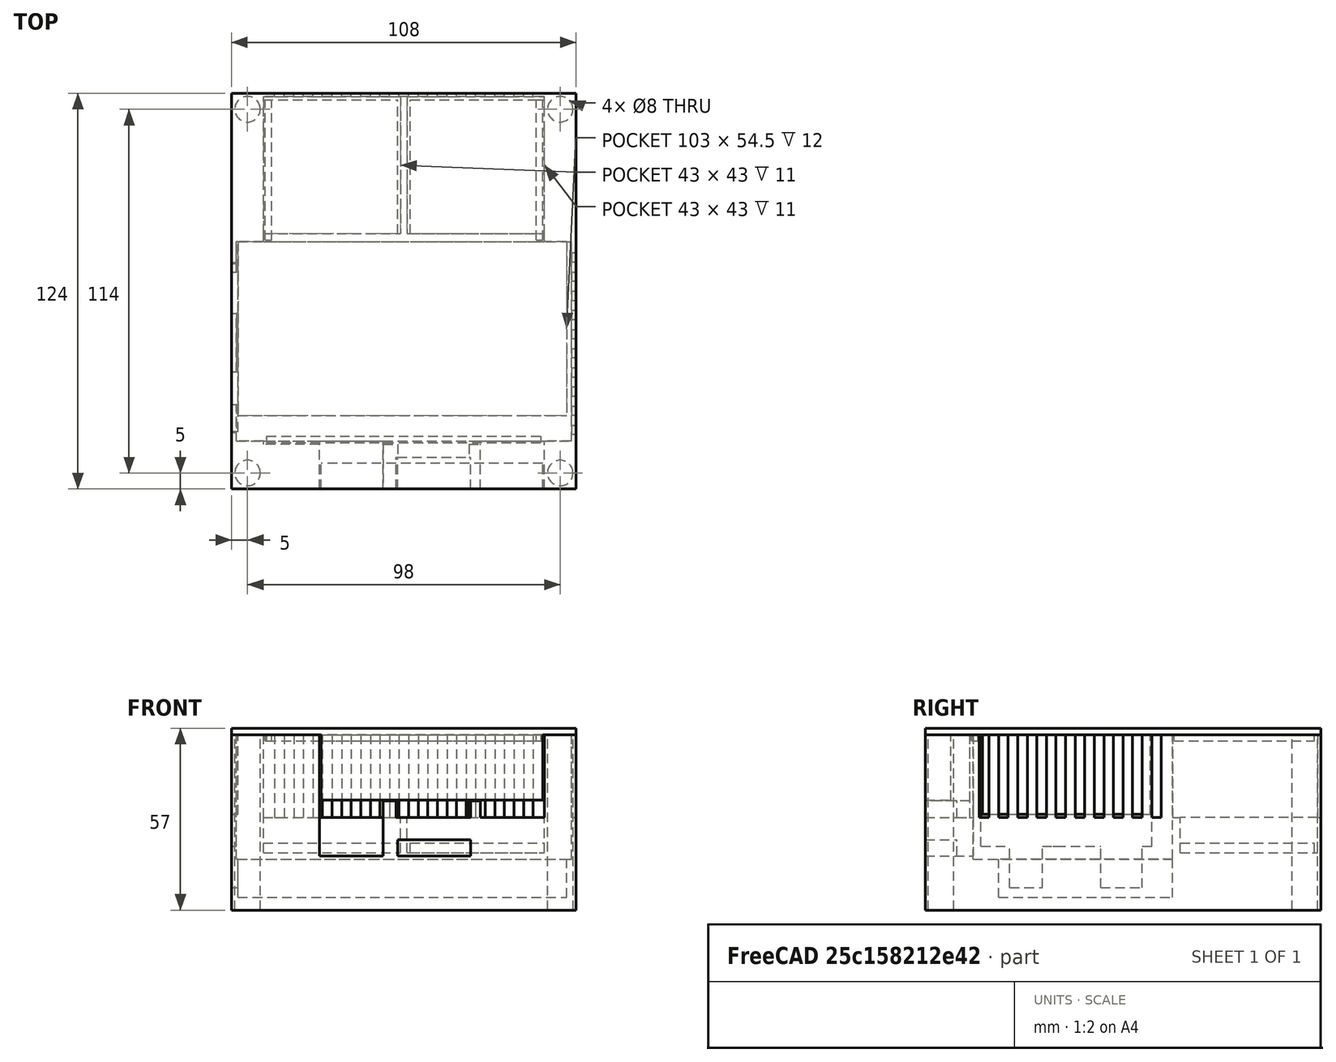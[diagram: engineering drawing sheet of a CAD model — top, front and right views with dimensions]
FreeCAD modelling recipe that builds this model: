
FCSTD DOCUMENT  (FreeCAD 0.19R24366 (Git))
Label: ORM-1 Controller Block
License: All rights reserved
LicenseURL: http://en.wikipedia.org/wiki/All_rights_reserved
objects: Part::Box×48, Part::Cut×15, Part::MultiFuse×6, Part::Cylinder×4, Mesh::Feature×2, App::MeasureDistance×2, Part::Compound×1
note: 74 computed .brp shape members not serialized (recipe doc carries the construction recipe); baked Part::Feature solids carry a one-line shape summary decoded from their .brp

FEATURE [Mesh::Feature] RAMPS1_4
  Placement = pos=(57,64,4) rot=(0,0,1;0rad)
FEATURE [Mesh::Feature] Fan_80mm
  Placement = pos=(6,13,84) rot=(0,0,1;0rad)
FEATURE [App::MeasureDistance] Distance  label="Distance: 78,43 mm"
  Distance = 78.426
  P1 = (81.5137,90.5618,25)
  P2 = (80.3884,12.1439,25)
FEATURE [Part::Box] Box  label="Encoders Jack"
  AttacherType = Attacher::AttachEngine3D
  Height = 5.08
  Length = 22.86
  Placement = pos=(52,0,17) rot=(0,0,1;0rad)
  Width = 10
  expr: Height = 2.54 * 2
  expr: Length = 2.54 * 9
FEATURE [Part::Box] Box001  label="ORM-1 CtrlBlock Main Volume"
  AttacherType = Attacher::AttachEngine3D
  Height = 55
  Length = 108
  Width = 124
FEATURE [Part::Box] Box002  label="A4988 Extension Board"
  AttacherType = Attacher::AttachEngine3D
  Height = 3
  Length = 42
  Placement = pos=(56,80,18) rot=(0,0,1;0rad)
  Width = 42
FEATURE [Part::Box] Box003  label="A4988 Extension Board001"
  AttacherType = Attacher::AttachEngine3D
  Height = 3
  Length = 42
  Placement = pos=(10,80,18) rot=(0,0,1;0rad)
  Width = 42
FEATURE [Part::Box] Box004  label="Arduino Board Socket"
  AttacherType = Attacher::AttachEngine3D
  Height = 100
  Length = 103
  Placement = pos=(2,23,4) rot=(0,0,1;0rad)
  Width = 54.5
FEATURE [Part::Cut] Cut  label="ORM-1 CTRL + ArduSocket"
  Base = -> Box001
  Tool = -> Box004
FEATURE [Part::Box] Box005  label="RAMPS1.4 Socket"
  AttacherType = Attacher::AttachEngine3D
  Height = 100
  Length = 105
  Placement = pos=(1.5,15,16) rot=(0,0,1;0rad)
  Width = 62.5
FEATURE [Part::Cut] Cut001  label="ORM-1 CTRL + Ramps Socket"
  Base = -> Cut
  Tool = -> Box005
FEATURE [Part::Box] Box006  label="A4988 Extension Board Socket"
  AttacherType = Attacher::AttachEngine3D
  Height = 100
  Length = 43
  Placement = pos=(55,80,18) rot=(0,0,1;0rad)
  Width = 43
FEATURE [Part::Box] Box007  label="A4988 Extension Board Socket001"
  AttacherType = Attacher::AttachEngine3D
  Height = 100
  Length = 43
  Placement = pos=(10,80,18) rot=(0,0,1;0rad)
  Width = 43
FEATURE [Part::Compound] Compound  label="A4988 Extension Board Sockets"
  Links = -> [Box006,Box007]
FEATURE [Part::Cut] Cut002  label="ORM-1 Controller Block. With A4988 Extension Board Sockets"
  Base = -> Cut001
  Tool = -> Compound
FEATURE [Part::Box] Box008  label="Encoders Jack Socket"
  AttacherType = Attacher::AttachEngine3D
  Height = 100
  Length = 23.36
  Placement = pos=(51.5,0,17) rot=(0,0,1;0rad)
  Width = 10
  expr: Length = 2.54 * 9 + 0.5
FEATURE [Part::Box] Box009  label="Encoders Jack Wires Socket"
  AttacherType = Attacher::AttachEngine3D
  Height = 100
  Length = 22.36
  Placement = pos=(52,0,17) rot=(0,0,1;0rad)
  Width = 16
  expr: Length = 2.54 * 9 - 0.5
FEATURE [Part::MultiFuse] Fusion  label="Encoder Jack Socket"
  Placement = pos=(0,0,12) rot=(0,0,1;0rad)
  Shapes = -> [Box008,Box009]
FEATURE [Part::Cut] Cut003  label="ORM-1 With Encoder Jack Socket"
  Base = -> Cut002
  Tool = -> Fusion
FEATURE [App::MeasureDistance] Distance001  label="Distance: 9,00 mm"
  Distance = 8.99628
  P1 = (69.3078,9.44422,17)
  P2 = (68.5344,0.481246,17)
FEATURE [Part::Box] Box010  label="Reset Button Socket"
  AttacherType = Attacher::AttachEngine3D
  Height = 100
  Length = 20
  Placement = pos=(27.5,0,17) rot=(0,0,1;0rad)
  Width = 17
FEATURE [Part::Cut] Cut004
  Base = -> Cut003
  Tool = -> Box010
FEATURE [Part::Box] Box011  label="USB Type B Socket"
  AttacherType = Attacher::AttachEngine3D
  Height = 100
  Length = 10
  Placement = pos=(0,55,7) rot=(0,0,1;0rad)
  Width = 13
FEATURE [Part::Cut] Cut005
  Base = -> Cut004
  Tool = -> Box011
FEATURE [Part::Box] Box012  label="Arduino Power Jack Socket"
  AttacherType = Attacher::AttachEngine3D
  Height = 100
  Length = 10
  Placement = pos=(0,26.5,7) rot=(0,0,1;0rad)
  Width = 10.2
FEATURE [Part::Cut] Cut006
  Base = -> Cut005
  Tool = -> Box012
FEATURE [Part::Box] Box013  label="RAMPS Input Power Socket"
  AttacherType = Attacher::AttachEngine3D
  Height = 100
  Length = 10
  Placement = pos=(0,17.5,20) rot=(0,0,1;0rad)
  Width = 23.5
FEATURE [Part::Cut] Cut007
  Base = -> Cut006
  Tool = -> Box013
FEATURE [Part::Box] Box014  label="RAMPS Output Power Socket"
  AttacherType = Attacher::AttachEngine3D
  Height = 100
  Length = 15
  Placement = pos=(0,40,20) rot=(0,0,1;0rad)
  Width = 31
FEATURE [Part::Cut] Cut008
  Base = -> Cut007
  Tool = -> Box014
FEATURE [Part::Box] Box015  label="Stepper Motors Wires Socket"
  AttacherType = Attacher::AttachEngine3D
  Height = 100
  Length = 20
  Placement = pos=(78,0,29) rot=(0,0,1;0rad)
  Width = 17
FEATURE [Part::Cut] Cut009
  Base = -> Cut008
  Tool = -> Box015
FEATURE [Part::Box] Box016  label="Excessive Volume Removal"
  AttacherType = Attacher::AttachEngine3D
  Height = 100
  Length = 88
  Placement = pos=(10,14,29) rot=(0,0,1;0rad)
  Width = 109
FEATURE [Part::Cut] Cut010
  Base = -> Cut009
  Tool = -> Box016
FEATURE [Part::Cylinder] Cylinder
  Angle = 360
  AttacherType = Attacher::AttachEngine3D
  Height = 100
  Placement = pos=(5,5,0) rot=(0,0,1;0rad)
  Radius = 4
FEATURE [Part::Cylinder] Cylinder001
  Angle = 360
  AttacherType = Attacher::AttachEngine3D
  Height = 100
  Placement = pos=(5,119,0) rot=(0,0,1;0rad)
  Radius = 4
FEATURE [Part::Cylinder] Cylinder002
  Angle = 360
  AttacherType = Attacher::AttachEngine3D
  Height = 100
  Placement = pos=(103,119,0) rot=(0,0,1;0rad)
  Radius = 4
FEATURE [Part::Cylinder] Cylinder003
  Angle = 360
  AttacherType = Attacher::AttachEngine3D
  Height = 100
  Placement = pos=(103,5,0) rot=(0,0,1;0rad)
  Radius = 4
FEATURE [Part::MultiFuse] Fusion001  label="Threaded Rivets Mounting Places"
  Shapes = -> [Cylinder,Cylinder001,Cylinder002,Cylinder003]
FEATURE [Part::Cut] Cut011
  Base = -> Cut010
  Tool = -> Fusion001
FEATURE [Part::Box] Box017  label="Extra Volume Removal"
  AttacherType = Attacher::AttachEngine3D
  Height = 100
  Length = 70.5
  Placement = pos=(27.5,0,34.2) rot=(0,0,1;0rad)
  Width = 19
  expr: .Placement.Base.z = 29 + 2.6 * 2
FEATURE [Part::Cut] Cut012
  Base = -> Cut011
  Tool = -> Box017
FEATURE [Part::Box] Box018  label="ORM-1 Controller Cover Main Volume"
  AttacherType = Attacher::AttachEngine3D
  Height = 2
  Length = 108
  Placement = pos=(0,0,55) rot=(0,0,1;0rad)
  Width = 124
FEATURE [Part::Box] Box019  label="Cube001"
  AttacherType = Attacher::AttachEngine3D
  Height = 21
  Length = 69.5
  Placement = pos=(28,0,34.5) rot=(0,0,1;0rad)
  Width = 8
FEATURE [Part::Box] Box020  label="Cube"
  AttacherType = Attacher::AttachEngine3D
  Height = 26
  Length = 2
  Placement = pos=(0,18,30) rot=(0,0,1;0rad)
  Width = 52.5
FEATURE [Part::Box] Box021  label="Cube002"
  AttacherType = Attacher::AttachEngine3D
  Height = 100
  Length = 10
  Placement = pos=(101,17,29) rot=(0,0,1;0rad)
  Width = 3
FEATURE [Part::Box] Box022  label="Cube003"
  AttacherType = Attacher::AttachEngine3D
  Height = 100
  Length = 10
  Placement = pos=(101,23,29) rot=(0,0,1;0rad)
  Width = 3
FEATURE [Part::Box] Box023  label="Cube004"
  AttacherType = Attacher::AttachEngine3D
  Height = 100
  Length = 10
  Placement = pos=(101,29,29) rot=(0,0,1;0rad)
  Width = 3
FEATURE [Part::Box] Box024  label="Cube005"
  AttacherType = Attacher::AttachEngine3D
  Height = 100
  Length = 10
  Placement = pos=(101,35,29) rot=(0,0,1;0rad)
  Width = 3
FEATURE [Part::Box] Box025  label="Cube006"
  AttacherType = Attacher::AttachEngine3D
  Height = 100
  Length = 10
  Placement = pos=(101,41,29) rot=(0,0,1;0rad)
  Width = 3
FEATURE [Part::Box] Box026  label="Cube007"
  AttacherType = Attacher::AttachEngine3D
  Height = 100
  Length = 10
  Placement = pos=(101,47,29) rot=(0,0,1;0rad)
  Width = 3
FEATURE [Part::Box] Box027  label="Cube008"
  AttacherType = Attacher::AttachEngine3D
  Height = 100
  Length = 10
  Placement = pos=(101,53,29) rot=(0,0,1;0rad)
  Width = 3
FEATURE [Part::Box] Box028  label="Cube009"
  AttacherType = Attacher::AttachEngine3D
  Height = 100
  Length = 10
  Placement = pos=(101,59,29) rot=(0,0,1;0rad)
  Width = 3
FEATURE [Part::Box] Box029  label="Cube010"
  AttacherType = Attacher::AttachEngine3D
  Height = 100
  Length = 10
  Placement = pos=(101,65,29) rot=(0,0,1;0rad)
  Width = 3
FEATURE [Part::Box] Box030  label="Cube011"
  AttacherType = Attacher::AttachEngine3D
  Height = 100
  Length = 10
  Placement = pos=(101,71,29) rot=(0,0,1;0rad)
  Width = 3
FEATURE [Part::MultiFuse] Fusion002  label="Ventilation 1"
  Shapes = -> [Box021,Box022,Box023,Box024,Box025,Box026,Box027,Box028,Box029,Box030]
FEATURE [Part::Cut] Cut013
  Base = -> Cut012
  Tool = -> Fusion002
FEATURE [Part::Box] Box031  label="Cube012"
  AttacherType = Attacher::AttachEngine3D
  Height = 100
  Length = 3
  Placement = pos=(13,119,29) rot=(0,0,1;0rad)
  Width = 10
FEATURE [Part::Box] Box032  label="Cube013"
  AttacherType = Attacher::AttachEngine3D
  Height = 100
  Length = 3
  Placement = pos=(19,119,29) rot=(0,0,1;0rad)
  Width = 10
FEATURE [Part::Box] Box033  label="Cube014"
  AttacherType = Attacher::AttachEngine3D
  Height = 100
  Length = 3
  Placement = pos=(25,119,29) rot=(0,0,1;0rad)
  Width = 10
FEATURE [Part::Box] Box034  label="Cube015"
  AttacherType = Attacher::AttachEngine3D
  Height = 100
  Length = 3
  Placement = pos=(31,119,29) rot=(0,0,1;0rad)
  Width = 10
FEATURE [Part::Box] Box035  label="Cube016"
  AttacherType = Attacher::AttachEngine3D
  Height = 100
  Length = 3
  Placement = pos=(37,119,29) rot=(0,0,1;0rad)
  Width = 10
FEATURE [Part::Box] Box036  label="Cube017"
  AttacherType = Attacher::AttachEngine3D
  Height = 100
  Length = 3
  Placement = pos=(43,119,29) rot=(0,0,1;0rad)
  Width = 10
FEATURE [Part::Box] Box037  label="Cube018"
  AttacherType = Attacher::AttachEngine3D
  Height = 100
  Length = 3
  Placement = pos=(49,119,29) rot=(0,0,1;0rad)
  Width = 10
FEATURE [Part::Box] Box038  label="Cube019"
  AttacherType = Attacher::AttachEngine3D
  Height = 100
  Length = 3
  Placement = pos=(55,119,29) rot=(0,0,1;0rad)
  Width = 10
FEATURE [Part::Box] Box039  label="Cube020"
  AttacherType = Attacher::AttachEngine3D
  Height = 100
  Length = 3
  Placement = pos=(61,119,29) rot=(0,0,1;0rad)
  Width = 10
FEATURE [Part::Box] Box040  label="Cube021"
  AttacherType = Attacher::AttachEngine3D
  Height = 100
  Length = 3
  Placement = pos=(67,119,29) rot=(0,0,1;0rad)
  Width = 10
FEATURE [Part::Box] Box041  label="Cube022"
  AttacherType = Attacher::AttachEngine3D
  Height = 100
  Length = 3
  Placement = pos=(73,119,29) rot=(0,0,1;0rad)
  Width = 10
FEATURE [Part::Box] Box042  label="Cube023"
  AttacherType = Attacher::AttachEngine3D
  Height = 100
  Length = 3
  Placement = pos=(79,119,29) rot=(0,0,1;0rad)
  Width = 10
FEATURE [Part::Box] Box043  label="Cube024"
  AttacherType = Attacher::AttachEngine3D
  Height = 100
  Length = 3
  Placement = pos=(85,119,29) rot=(0,0,1;0rad)
  Width = 10
FEATURE [Part::Box] Box044  label="Cube025"
  AttacherType = Attacher::AttachEngine3D
  Height = 100
  Length = 3
  Placement = pos=(91,119,29) rot=(0,0,1;0rad)
  Width = 10
FEATURE [Part::MultiFuse] Fusion003  label="Ventilation2"
  Placement = pos=(0.5,0,0) rot=(0,0,1;0rad)
  Shapes = -> [Box031,Box032,Box033,Box034,Box035,Box036,Box037,Box038,Box039,Box040,Box041,Box042,Box043,Box044]
FEATURE [Part::Cut] Cut014
  Base = -> Cut013
  Tool = -> Fusion003
FEATURE [Part::Box] Box045  label="Cube026"
  AttacherType = Attacher::AttachEngine3D
  Height = 2
  Length = 2
  Placement = pos=(10.5,78,53) rot=(0,0,1;0rad)
  Width = 44
FEATURE [Part::Box] Box046  label="Cube027"
  AttacherType = Attacher::AttachEngine3D
  Height = 2
  Length = 2
  Placement = pos=(95.5,78,53) rot=(0,0,1;0rad)
  Width = 44
FEATURE [Part::Box] Box047  label="Cube028"
  AttacherType = Attacher::AttachEngine3D
  Height = 2
  Length = 86
  Placement = pos=(11,14.5,53) rot=(0,0,1;0rad)
  Width = 2
FEATURE [Part::MultiFuse] Fusion004  label="CoverSalients"
  Shapes = -> [Box019,Box020,Box045,Box046,Box047]
FEATURE [Part::MultiFuse] Fusion005
  Shapes = -> [Box018,Fusion004]
